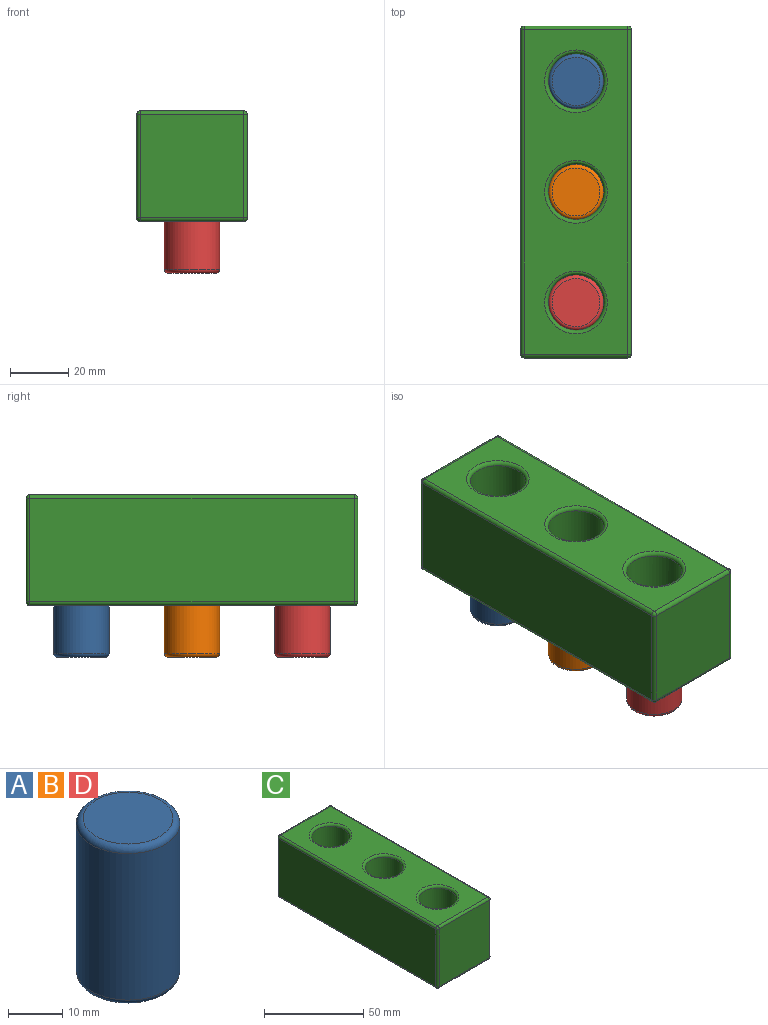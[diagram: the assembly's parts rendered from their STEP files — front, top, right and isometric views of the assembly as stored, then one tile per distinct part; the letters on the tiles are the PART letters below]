
ASSEMBLY  parts=4 mates=3
PART A: 5 faces, bbox 20.6x20.6x35.6 mm
  f0: cylinder r=9.53mm len=33.02mm, axis (0,0,-1), area 1976.2mm2, adj f3,f4
  f1: plane 16.51x16.51mm, normal (0,0,1), area 214.1mm2, adj f4
  f2: plane 16.51x16.51mm, normal (0,0,-1), area 214.1mm2, adj f3
  f3: torus R=8.26mm, axis (0,0,1), area 113.6mm2, adj f0,f2
  f4: torus R=8.26mm, axis (0,0,1), area 113.6mm2, adj f0,f1
PART B: same geometry as A
PART C: 32 faces, bbox 38.1x114.3x38.1 mm
  f0: plane 111.76x35.56mm, normal (0,0,-1), area 3119.1mm2, adj f14,f19,f22,f25,f26,f27,f28
  f1: plane 111.76x35.56mm, normal (1,0,0), area 3974.2mm2, adj f11,f20,f21,f25
  f2: plane 111.76x35.56mm, normal (0,0,1), area 2875.9mm2, adj f6,f10,f11,f12,f29,f30,f31
  f3: plane 111.76x35.56mm, normal (-1,0,0), area 3974.2mm2, adj f6,f9,f13,f14
  f4: plane 35.56x35.56mm, normal (0,-1,0), area 1264.5mm2, adj f9,f10,f19,f20
  f5: plane 35.56x35.56mm, normal (0,1,0), area 1264.5mm2, adj f12,f13,f21,f22
  f6: cylinder r=1.27mm len=111.76mm, axis (0,1,0), area 223mm2, adj f2,f3,f7,f8
  f7: sphere r=1.27mm, area 2.5mm2, adj f6,f9,f10
  f8: sphere r=1.27mm, area 2.5mm2, adj f6,f12,f13
  f9: cylinder r=1.27mm len=35.56mm, axis (0,0,1), area 70.9mm2, adj f3,f4,f7,f15
  f10: cylinder r=1.27mm len=35.56mm, axis (1,0,0), area 70.9mm2, adj f2,f4,f7,f16
  f11: cylinder r=1.27mm len=111.76mm, axis (0,-1,0), area 223mm2, adj f1,f2,f16,f17
  f12: cylinder r=1.27mm len=35.56mm, axis (-1,0,0), area 70.9mm2, adj f2,f5,f8,f17
  f13: cylinder r=1.27mm len=35.56mm, axis (0,0,-1), area 70.9mm2, adj f3,f5,f8,f18
  f14: cylinder r=1.27mm len=111.76mm, axis (0,-1,0), area 223mm2, adj f0,f3,f15,f18
  f15: sphere r=1.27mm, area 2.5mm2, adj f9,f14,f19
  f16: sphere r=1.27mm, area 2.5mm2, adj f10,f11,f20
  f17: sphere r=1.27mm, area 2.5mm2, adj f11,f12,f21
  f18: sphere r=1.27mm, area 2.5mm2, adj f13,f14,f22
  f19: cylinder r=1.27mm len=35.56mm, axis (-1,0,0), area 70.9mm2, adj f0,f4,f15,f23
  f20: cylinder r=1.27mm len=35.56mm, axis (0,0,-1), area 70.9mm2, adj f1,f4,f16,f23
  f21: cylinder r=1.27mm len=35.56mm, axis (0,0,1), area 70.9mm2, adj f1,f5,f17,f24
  f22: cylinder r=1.27mm len=35.56mm, axis (1,0,0), area 70.9mm2, adj f0,f5,f18,f24
  f23: sphere r=1.27mm, area 2.5mm2, adj f19,f20,f25
  f24: sphere r=1.27mm, area 2.5mm2, adj f21,f22,f25
  f25: cylinder r=1.27mm len=111.76mm, axis (0,1,0), area 223mm2, adj f0,f1,f23,f24
  f26: cylinder r=9.53mm len=36.83mm, axis (0,0,1), area 2204.2mm2, adj f0,f29
  f27: cylinder r=9.53mm len=36.83mm, axis (0,0,1), area 2204.2mm2, adj f0,f30
  f28: cylinder r=9.53mm len=36.83mm, axis (0,0,1), area 2204.2mm2, adj f0,f31
  f29: torus R=10.79mm, axis (0,0,-1), area 125.2mm2, adj f2,f26
  f30: torus R=10.79mm, axis (0,0,-1), area 125.2mm2, adj f2,f27
  f31: torus R=10.79mm, axis (0,0,-1), area 125.2mm2, adj f2,f28
PART D: same geometry as A
PLACE A t=(0,-19.05,-36.83)mm
PLACE B t=(0,-57.15,-36.83)mm
PLACE C at identity fixed
PLACE D t=(0,-95.25,-36.83)mm
MATE fastened D.f0 <-> C.f27  axis (0,0,-1) through (0,-95.25,-19.05)mm
MATE fastened A.f0 <-> C.f28  axis (0,0,-1) through (0,-19.05,-19.05)mm
MATE fastened B.f0 <-> C.f26  axis (0,0,-1) through (0,-57.15,-19.05)mm
